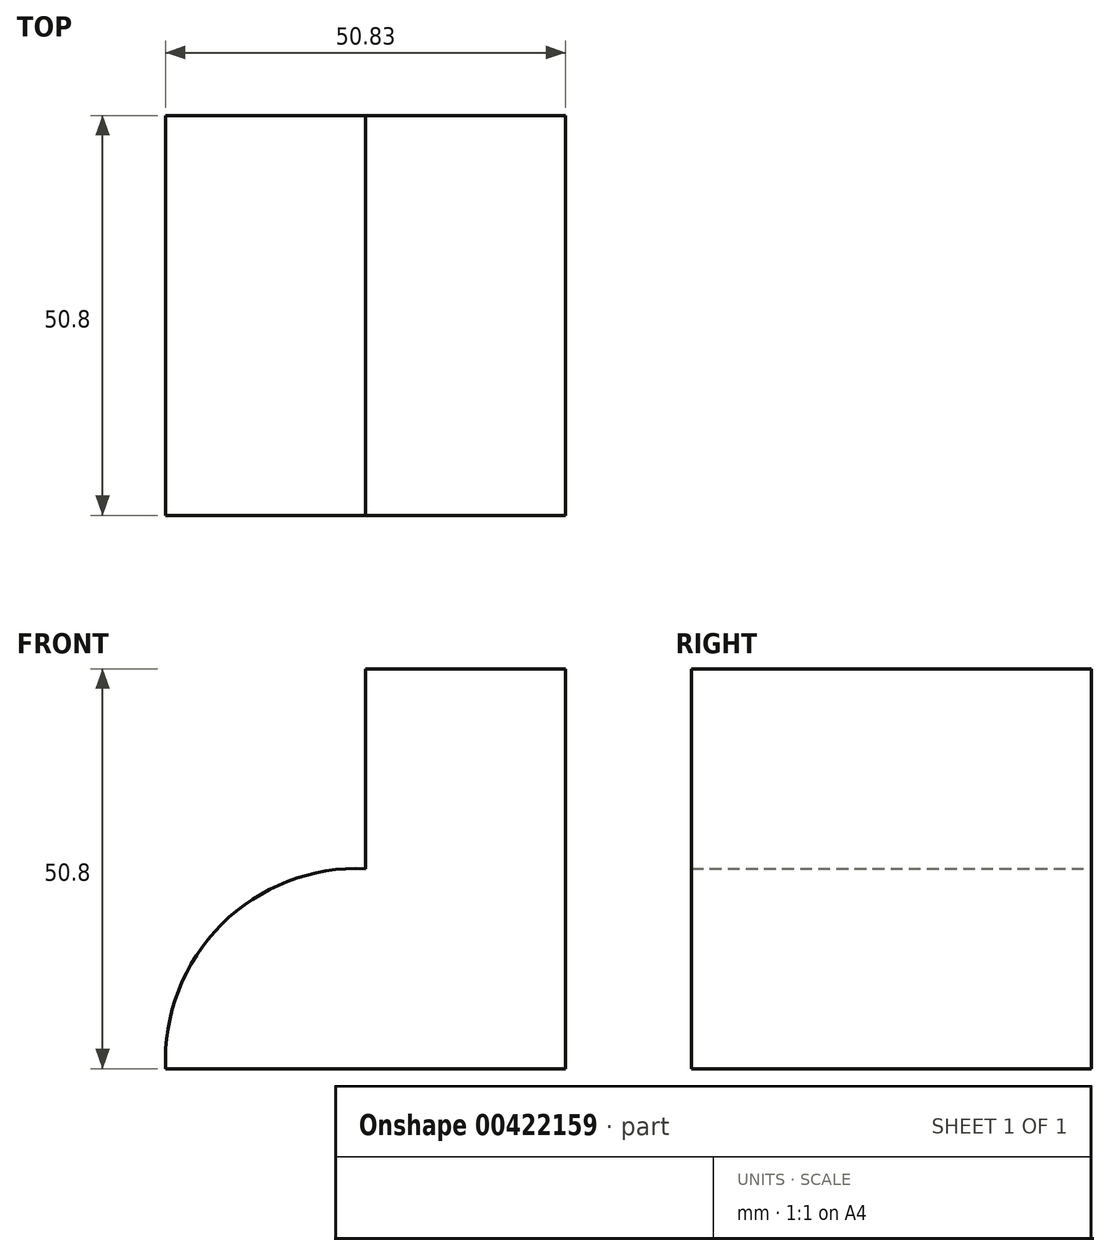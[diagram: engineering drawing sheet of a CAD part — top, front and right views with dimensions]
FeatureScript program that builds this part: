
annotation { "Feature Type Name" : "Feature", "Feature Type Description" : "" }
export const myFeature = defineFeature(function(context is Context, id is Id, definition is map)
    precondition{}
    {
        {
            var Q0;
            Q0=qCreatedBy(makeId("Front.planeOp"),FACE);
            var sketch = newSketch(context, id + "F0", { "sketchPlane" : qUnion([Q0])});
            skLineSegment(sketch, "E0", {"start": v(-19.98, 41.48) * mm, "end": v(-19.98, 16.08) * mm});
            skLineSegment(sketch, "E1", {"start": v(-19.98, 41.48) * mm, "end": v(5.42, 41.48) * mm});
            skLineSegment(sketch, "E2", {"start": v(5.42, 41.48) * mm, "end": v(5.42, -9.32) * mm});
            skLineSegment(sketch, "E3", {"start": v(5.42, -9.32) * mm, "end": v(-45.38, -9.32) * mm});
            skArc(sketch, "E4", {"start": v(-19.98, 16.08) * mm, "mid": v(-38.3, 9) * mm, "end": v(-45.38, -9.32) * mm});
            skSolve(sketch);
        }
        {
            var Q0;
            Q0 = qSketchRegion(id + "F0", true);
            extrude(context, id + "F1", {"entities" : qUnion([Q0]), "depth" : 50.8 * mm});
        }
    });
